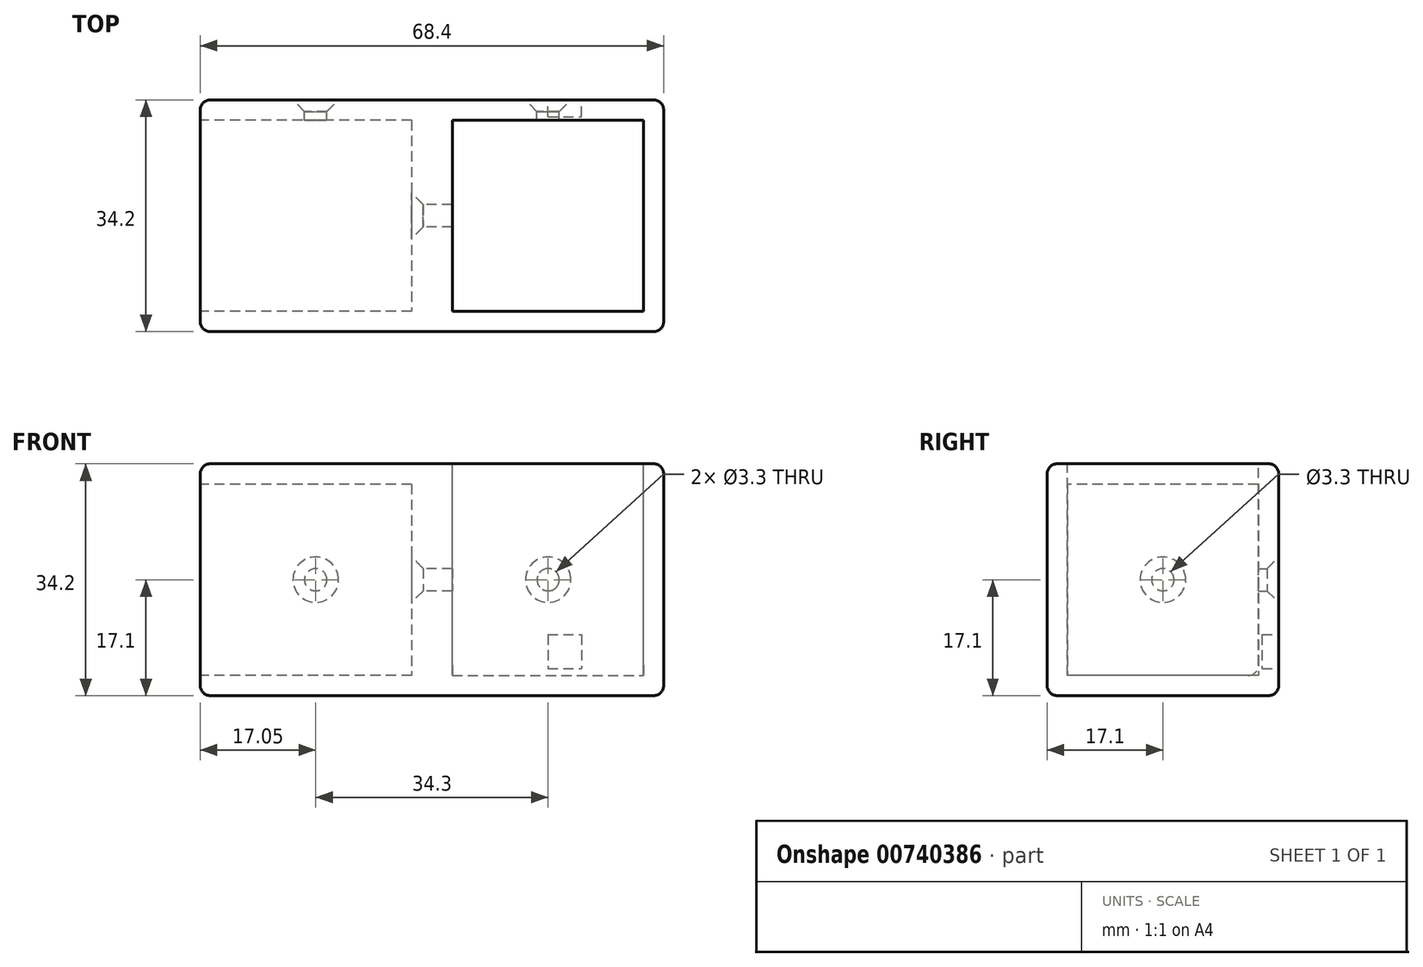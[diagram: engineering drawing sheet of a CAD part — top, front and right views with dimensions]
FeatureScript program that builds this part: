
annotation { "Feature Type Name" : "Feature", "Feature Type Description" : "" }
export const myFeature = defineFeature(function(context is Context, id is Id, definition is map)
    precondition{}
    {
        {
            var Q0;
            Q0=qCreatedBy(makeId("Top.planeOp"),FACE);
            var sketch = newSketch(context, id + "F0", { "sketchPlane" : qUnion([Q0])});
            skLineSegment(sketch, "E0.bottom", {"start": v(-8, 0) * mm, "end": v(-34.2, 0) * mm});
            skLineSegment(sketch, "E0.top", {"start": v(0, 34.2) * mm, "end": v(-34.2, 34.2) * mm});
            skLineSegment(sketch, "E0.left", {"start": v(0, 0) * mm, "end": v(0, 34.2) * mm});
            skLineSegment(sketch, "E0.right", {"start": v(-34.2, 0) * mm, "end": v(-34.2, 34.2) * mm});
            skLineSegment(sketch, "E1", {"start": v(0, 0) * mm, "end": v(-8, 0) * mm});
            skSolve(sketch);
        }
        {
            var Q0;
            Q0=makeQuery(id+"F0.imprint","IMPRINT",FACE,{"disambiguationData":[TD([[makeQuery(id+"F0.imprint","IMPRINT",EDGE,{"derivedFrom":sQuery(id+"F0.wireOp",EDGE,"E0.bottom")}),-1.0]])]});
            var Q1;
            Q1=makeQuery(id+"F0.imprint","IMPRINT",FACE,{"disambiguationData":[TD([[makeQuery(id+"F0.imprint","IMPRINT",EDGE,{"derivedFrom":sQuery(id+"F0.wireOp",EDGE,"QRwr5Akg-HTZL-sOMh-trkn-U98YefTGLHnr")}),1.0]])]});
            extrude(context, id + "F1", {"entities" : qUnion([Q0, Q1]), "depth" : 34.2 * mm, "offsetDistance" : 25 * mm});
        }
        {
            var Q0;
            Q0=makeQuery(id+"F1.opExtrude","CAP_FACE",FACE,{"disambiguationData":[OSD([sQuery(id+"F0.wireOp",EDGE,"E0.bottom"),sQuery(id+"F0.wireOp",EDGE,"E0.top"),sQuery(id+"F0.wireOp",EDGE,"E0.left"),sQuery(id+"F0.wireOp",EDGE,"E0.right"),sQuery(id+"F0.wireOp",EDGE,"QRwr5Akg-HTZL-sOMh-trkn-U98YefTGLHnr"),sQuery(id+"F0.wireOp",EDGE,"6FfksXsB-Y7vq-xAn0-bQFg-GBrETYwM94Cl"),sQuery(id+"F0.wireOp",EDGE,"N7Ms4oqh-Htai-qQox-I7Rp-QqMJWiCJs41g"),sQuery(id+"F0.wireOp",EDGE,"P6Kv1fKs-vESP-vTW7-nFhL-l93CeoGK7j3d")])],"isStart":false});
            var sketch = newSketch(context, id + "F2", { "sketchPlane" : qUnion([Q0])});
            skLineSegment(sketch, "E2.bottom", {"start": v(-34.2, 34.2) * mm, "end": v(0, 34.2) * mm});
            skLineSegment(sketch, "E2.top", {"start": v(-34.2, 0) * mm, "end": v(0, 0) * mm});
            skLineSegment(sketch, "E2.left", {"start": v(-34.2, 34.2) * mm, "end": v(-34.2, 0) * mm});
            skLineSegment(sketch, "E2.right", {"start": v(0, 34.2) * mm, "end": v(0, 0) * mm});
            skLineSegment(sketch, "E3.0", {"start": v(-31.2, 31.2) * mm, "end": v(-3, 31.2) * mm});
            skLineSegment(sketch, "E3.1", {"start": v(-31.2, 31.2) * mm, "end": v(-31.2, 3) * mm});
            skLineSegment(sketch, "E3.2", {"start": v(-31.2, 3) * mm, "end": v(-3, 3) * mm});
            skLineSegment(sketch, "E3.3", {"start": v(-3, 31.2) * mm, "end": v(-3, 3) * mm});
            skSolve(sketch);
        }
        {
            var Q0;
            Q0=makeQuery(id+"F2.imprint","IMPRINT",FACE,{"disambiguationData":[TD([[makeQuery(id+"F2.imprint","IMPRINT",EDGE,{"derivedFrom":sQuery(id+"F2.wireOp",EDGE,"E3.0")}),-1.0]])]});
            extrude(context, id + "F3", {"entities" : qUnion([Q0]), "operationType" : NewBodyOperationType.REMOVE, "oppositeDirection" : true, "depth" : 31.2 * mm, "offsetDistance" : 25 * mm});
        }
        {
            var Q0;
            Q0=makeQuery(id+"F1.opExtrude","SWEPT_FACE",FACE,{"disambiguationData":[OSD([sQuery(id+"F0.wireOp",EDGE,"E0.right")])]});
            var sketch = newSketch(context, id + "F4", { "sketchPlane" : qUnion([Q0])});
            skLineSegment(sketch, "E4.bottom", {"start": v(-34.2, 0) * mm, "end": v(0, 0) * mm});
            skLineSegment(sketch, "E4.top", {"start": v(-34.2, 34.2) * mm, "end": v(0, 34.2) * mm});
            skLineSegment(sketch, "E4.left", {"start": v(-34.2, 0) * mm, "end": v(-34.2, 34.2) * mm});
            skLineSegment(sketch, "E4.right", {"start": v(0, 0) * mm, "end": v(0, 34.2) * mm});
            skSolve(sketch);
        }
        {
            var Q0;
            Q0=qSketchRegion(id+"F4",true);
            extrude(context, id + "F5", {"entities" : qUnion([Q0]), "operationType" : NewBodyOperationType.ADD, "depth" : 34.2 * mm, "offsetDistance" : 25 * mm});
        }
        {
            var Q0;
            Q0=makeQuery(id+"F5.opExtrude","CAP_FACE",FACE,{"disambiguationData":[OSD([sQuery(id+"F4.wireOp",EDGE,"E4.bottom"),sQuery(id+"F4.wireOp",EDGE,"E4.top"),sQuery(id+"F4.wireOp",EDGE,"E4.left"),sQuery(id+"F4.wireOp",EDGE,"E4.right")])],"isStart":false});
            var sketch = newSketch(context, id + "F6", { "sketchPlane" : qUnion([Q0])});
            skLineSegment(sketch, "E5.bottom", {"start": v(-34.2, 34.2) * mm, "end": v(0, 34.2) * mm});
            skLineSegment(sketch, "E5.top", {"start": v(-34.2, 0) * mm, "end": v(0, 0) * mm});
            skLineSegment(sketch, "E5.left", {"start": v(-34.2, 34.2) * mm, "end": v(-34.2, 0) * mm});
            skLineSegment(sketch, "E5.right", {"start": v(0, 34.2) * mm, "end": v(0, 0) * mm});
            skLineSegment(sketch, "E6.0", {"start": v(-31.2, 31.2) * mm, "end": v(-3, 31.2) * mm});
            skLineSegment(sketch, "E6.1", {"start": v(-31.2, 31.2) * mm, "end": v(-31.2, 3) * mm});
            skLineSegment(sketch, "E6.2", {"start": v(-31.2, 3) * mm, "end": v(-3, 3) * mm});
            skLineSegment(sketch, "E6.3", {"start": v(-3, 31.2) * mm, "end": v(-3, 3) * mm});
            skSolve(sketch);
        }
        {
            var Q0;
            Q0=makeQuery(id+"F6.imprint","IMPRINT",FACE,{"disambiguationData":[TD([[makeQuery(id+"F6.imprint","IMPRINT",EDGE,{"derivedFrom":sQuery(id+"F6.wireOp",EDGE,"E6.0")}),-1.0]])]});
            extrude(context, id + "F7", {"entities" : qUnion([Q0]), "operationType" : NewBodyOperationType.REMOVE, "oppositeDirection" : true, "depth" : 31.2 * mm, "offsetDistance" : 25 * mm});
        }
        {
            var Q0;
            Q0=makeQuery(id+"F5.boolean.opBoolean","MERGE",FACE,{"derivedFrom":[makeQuery(id+"F1.opExtrude","SWEPT_FACE",FACE,{"disambiguationData":[OSD([sQuery(id+"F0.wireOp",EDGE,"E0.top")])]}),makeQuery(id+"F5.opExtrude","SWEPT_FACE",FACE,{"disambiguationData":[OSD([sQuery(id+"F4.wireOp",EDGE,"E4.left")])]})]});
            var sketch = newSketch(context, id + "F8", { "sketchPlane" : qUnion([Q0])});
            skPoint(sketch, "E7", {"position": v(17.05, 17.1) * mm});
            skPoint(sketch, "E8", {"position": v(51.35, 17.1) * mm});
            skSolve(sketch);
        }
        {
            var Q0;
            Q0=makeQuery(id+"F7.boolean.opBoolean","COPY",FACE,{"derivedFrom":makeQuery(id+"F7.opExtrude","CAP_FACE",FACE,{"disambiguationData":[OSD([sQuery(id+"F6.wireOp",EDGE,"E6.0"),sQuery(id+"F6.wireOp",EDGE,"E6.1"),sQuery(id+"F6.wireOp",EDGE,"E6.2"),sQuery(id+"F6.wireOp",EDGE,"E6.3")])],"isStart":false})});
            var sketch = newSketch(context, id + "F9", { "sketchPlane" : qUnion([Q0])});
            skPoint(sketch, "E9", {"position": v(-17.1, 17.1) * mm});
            skSolve(sketch);
        }
        {
            var Q0;
            Q0=sQuery(id+"F8.wireOp",VERTEX,"E7");
            var Q1;
            Q1=sQuery(id+"F8.wireOp",VERTEX,"E8");
            var Q2;
            Q2=sQuery(id+"F9.wireOp",VERTEX,"E9");
            var Q3;
            Q3=makeQuery(id+"F1.opExtrude","SWEPT_BODY",BODY,{"disambiguationData":[OSD([sQuery(id+"F0.wireOp",EDGE,"E0.bottom"),sQuery(id+"F0.wireOp",EDGE,"E0.top"),sQuery(id+"F0.wireOp",EDGE,"E0.left"),sQuery(id+"F0.wireOp",EDGE,"E0.right"),sQuery(id+"F0.wireOp",EDGE,"QRwr5Akg-HTZL-sOMh-trkn-U98YefTGLHnr"),sQuery(id+"F0.wireOp",EDGE,"6FfksXsB-Y7vq-xAn0-bQFg-GBrETYwM94Cl"),sQuery(id+"F0.wireOp",EDGE,"N7Ms4oqh-Htai-qQox-I7Rp-QqMJWiCJs41g"),sQuery(id+"F0.wireOp",EDGE,"P6Kv1fKs-vESP-vTW7-nFhL-l93CeoGK7j3d")])]});
            hole(context, id + "F10", {"style" : HoleStyle.C_SINK, "endStyle" : HoleEndStyle.BLIND, "standardTappedOrClearance" : lookupTablePath({ "standard" : "ISO", "fit" : "Normal", "size" : "M3", "type" : "Clearance" }), "standardBlindInLast" : lookupTablePath({ "fit" : "Standard", "standard" : "ISO", "size" : "M3", "type" : "Clearance" }), "holeDiameter" : 3.3 * mm, "cSinkDiameter" : 6.72 * mm, "cSinkAngle" : 90 * degree, "majorDiameter" : 5 * mm, "holeDepth" : 25 * mm, "isTappedThrough" : true, "tappedDepth" : 12 * mm, "tapClearance" : 3, "startFromSketch" : true, "locations" : qUnion([Q0, Q1, Q2]), "scope" : qUnion([Q3])});
        }
        {
            var Q0;
            Q0=makeQuery(id+"F3.boolean.opBoolean","COPY",EDGE,{"derivedFrom":makeQuery(id+"F3.opExtrude","CAP_EDGE",EDGE,{"disambiguationData":[OSD([sQuery(id+"F2.wireOp",EDGE,"E3.1")])],"isStart":true})});
            var Q1;
            Q1=makeQuery(id+"F3.boolean.opBoolean","COPY",EDGE,{"derivedFrom":makeQuery(id+"F3.opExtrude","CAP_EDGE",EDGE,{"disambiguationData":[OSD([sQuery(id+"F2.wireOp",EDGE,"E3.0")])],"isStart":true})});
            var Q2;
            Q2=makeQuery(id+"F3.boolean.opBoolean","COPY",EDGE,{"derivedFrom":makeQuery(id+"F3.opExtrude","CAP_EDGE",EDGE,{"disambiguationData":[OSD([sQuery(id+"F2.wireOp",EDGE,"E3.0")])],"isStart":false})});
            var Q3;
            Q3=makeQuery(id+"F1.opExtrude","CAP_EDGE",EDGE,{"disambiguationData":[OSD([sQuery(id+"F0.wireOp",EDGE,"E0.left"),sQuery(id+"F0.wireOp",EDGE,"N7Ms4oqh-Htai-qQox-I7Rp-QqMJWiCJs41g")])],"isStart":false});
            var Q4;
            Q4=makeQuery(id+"F5.boolean.opBoolean","MERGE",EDGE,{"derivedFrom":[makeQuery(id+"F1.opExtrude","CAP_EDGE",EDGE,{"disambiguationData":[OSD([sQuery(id+"F0.wireOp",EDGE,"E0.bottom")])],"isStart":false}),makeQuery(id+"F5.opExtrude","SWEPT_EDGE",EDGE,{"disambiguationData":[OSD([sQuery(id+"F4.wireOp",EDGE,"E4.top"),sQuery(id+"F4.wireOp",EDGE,"E4.right")])]})]});
            var Q5;
            Q5=makeQuery(id+"F5.opExtrude","CAP_EDGE",EDGE,{"disambiguationData":[OSD([sQuery(id+"F4.wireOp",EDGE,"E4.top")])],"isStart":false});
            var Q6;
            Q6=makeQuery(id+"F5.boolean.opBoolean","MERGE",EDGE,{"derivedFrom":[makeQuery(id+"F1.opExtrude","CAP_EDGE",EDGE,{"disambiguationData":[OSD([sQuery(id+"F0.wireOp",EDGE,"E0.top")])],"isStart":false}),makeQuery(id+"F5.opExtrude","SWEPT_EDGE",EDGE,{"disambiguationData":[OSD([sQuery(id+"F4.wireOp",EDGE,"E4.top"),sQuery(id+"F4.wireOp",EDGE,"E4.left")])]})]});
            var Q7;
            Q7=makeQuery(id+"F1.opExtrude","SWEPT_EDGE",EDGE,{"disambiguationData":[OSD([sQuery(id+"F0.wireOp",EDGE,"E0.top"),sQuery(id+"F0.wireOp",EDGE,"E0.left")])]});
            var Q8;
            Q8=makeQuery(id+"F7.boolean.opBoolean","COPY",EDGE,{"derivedFrom":makeQuery(id+"F7.opExtrude","CAP_EDGE",EDGE,{"disambiguationData":[OSD([sQuery(id+"F6.wireOp",EDGE,"E6.0")])],"isStart":true})});
            var Q9;
            Q9=makeQuery(id+"F5.opExtrude","CAP_EDGE",EDGE,{"disambiguationData":[OSD([sQuery(id+"F4.wireOp",EDGE,"E4.right")])],"isStart":false});
            var Q10;
            Q10=makeQuery(id+"F7.boolean.opBoolean","COPY",EDGE,{"derivedFrom":makeQuery(id+"F7.opExtrude","CAP_EDGE",EDGE,{"disambiguationData":[OSD([sQuery(id+"F6.wireOp",EDGE,"E6.3")])],"isStart":true})});
            var Q11;
            Q11=makeQuery(id+"F7.boolean.opBoolean","COPY",EDGE,{"derivedFrom":makeQuery(id+"F7.opExtrude","CAP_EDGE",EDGE,{"disambiguationData":[OSD([sQuery(id+"F6.wireOp",EDGE,"E6.1")])],"isStart":true})});
            var Q12;
            Q12=makeQuery(id+"F5.opExtrude","CAP_EDGE",EDGE,{"disambiguationData":[OSD([sQuery(id+"F4.wireOp",EDGE,"E4.left")])],"isStart":false});
            var Q13;
            Q13=makeQuery(id+"F7.boolean.opBoolean","COPY",EDGE,{"derivedFrom":makeQuery(id+"F7.opExtrude","CAP_EDGE",EDGE,{"disambiguationData":[OSD([sQuery(id+"F6.wireOp",EDGE,"E6.2")])],"isStart":true})});
            var Q14;
            Q14=makeQuery(id+"F5.opExtrude","CAP_EDGE",EDGE,{"disambiguationData":[OSD([sQuery(id+"F4.wireOp",EDGE,"E4.bottom")])],"isStart":false});
            var Q15;
            Q15=makeQuery(id+"F5.boolean.opBoolean","MERGE",EDGE,{"derivedFrom":[makeQuery(id+"F1.opExtrude","CAP_EDGE",EDGE,{"disambiguationData":[OSD([sQuery(id+"F0.wireOp",EDGE,"E0.bottom")])],"isStart":true}),makeQuery(id+"F5.opExtrude","SWEPT_EDGE",EDGE,{"disambiguationData":[OSD([sQuery(id+"F4.wireOp",EDGE,"E4.bottom"),sQuery(id+"F4.wireOp",EDGE,"E4.right")])]})]});
            var Q16;
            Q16=makeQuery(id+"F5.boolean.opBoolean","MERGE",EDGE,{"derivedFrom":[makeQuery(id+"F1.opExtrude","CAP_EDGE",EDGE,{"disambiguationData":[OSD([sQuery(id+"F0.wireOp",EDGE,"E0.top")])],"isStart":true}),makeQuery(id+"F5.opExtrude","SWEPT_EDGE",EDGE,{"disambiguationData":[OSD([sQuery(id+"F4.wireOp",EDGE,"E4.bottom"),sQuery(id+"F4.wireOp",EDGE,"E4.left")])]})]});
            var Q17;
            Q17=makeQuery(id+"F1.opExtrude","SWEPT_EDGE",EDGE,{"disambiguationData":[OSD([sQuery(id+"F0.wireOp",EDGE,"E0.left"),sQuery(id+"F0.wireOp",EDGE,"E1")])]});
            var Q18;
            Q18=makeQuery(id+"F3.boolean.opBoolean","COPY",EDGE,{"derivedFrom":makeQuery(id+"F3.opExtrude","CAP_EDGE",EDGE,{"disambiguationData":[OSD([sQuery(id+"F2.wireOp",EDGE,"E3.3")])],"isStart":true})});
            var Q19;
            Q19=makeQuery(id+"F3.boolean.opBoolean","COPY",EDGE,{"derivedFrom":makeQuery(id+"F3.opExtrude","CAP_EDGE",EDGE,{"disambiguationData":[OSD([sQuery(id+"F2.wireOp",EDGE,"E3.2")])],"isStart":true})});
            var Q20;
            Q20=makeQuery(id+"F1.opExtrude","CAP_EDGE",EDGE,{"disambiguationData":[OSD([sQuery(id+"F0.wireOp",EDGE,"E0.left")])],"isStart":true});
            fillet(context, id + "F11", {"entities" : qUnion([Q0, Q1, Q2, Q3, Q4, Q5, Q6, Q7, Q8, Q9, Q10, Q11, Q12, Q13, Q14, Q15, Q16, Q17, Q18, Q19, Q20]), "radius" : 1.5 * mm, "tangentPropagation" : true, "allowEdgeOverflow" : false});
        }
        {
            var Q0;
            {var subQ1=sQuery(id+"F4.wireOp",EDGE,"E4.left");Q0=makeQuery(id+"F8.imprint","IMPRINT",FACE,{"disambiguationData":[TD([[makeQuery(id+"F8.imprint","IMPRINT",EDGE,{"derivedFrom":makeQuery(id+"F5.opExtrude","CAP_EDGE",EDGE,{"disambiguationData":[OSD([subQ1])],"isStart":false})}),-1.0]])]});}
            var sketch = newSketch(context, id + "F12", { "sketchPlane" : qUnion([Q0])});
            skPoint(sketch, "E10", {"position": v(14.6, 6.5) * mm});
            skLineSegment(sketch, "E11.bottom", {"start": v(17.1, 9) * mm, "end": v(12.1, 9) * mm});
            skLineSegment(sketch, "E11.top", {"start": v(17.1, 4) * mm, "end": v(12.1, 4) * mm});
            skLineSegment(sketch, "E11.left", {"start": v(17.1, 9) * mm, "end": v(17.1, 4) * mm});
            skLineSegment(sketch, "E11.right", {"start": v(12.1, 9) * mm, "end": v(12.1, 4) * mm});
            skSolve(sketch);
        }
        {
            var Q0;
            Q0=makeQuery(id+"F12.imprint","IMPRINT",FACE,{"disambiguationData":[TD([[makeQuery(id+"F12.imprint","IMPRINT",EDGE,{"derivedFrom":sQuery(id+"F12.wireOp",EDGE,"E11.bottom")}),1.0]])]});
            extrude(context, id + "F13", {"entities" : qUnion([Q0]), "operationType" : NewBodyOperationType.REMOVE, "oppositeDirection" : true, "depth" : 2.5 * mm, "offsetDistance" : 25 * mm});
        }
    });
